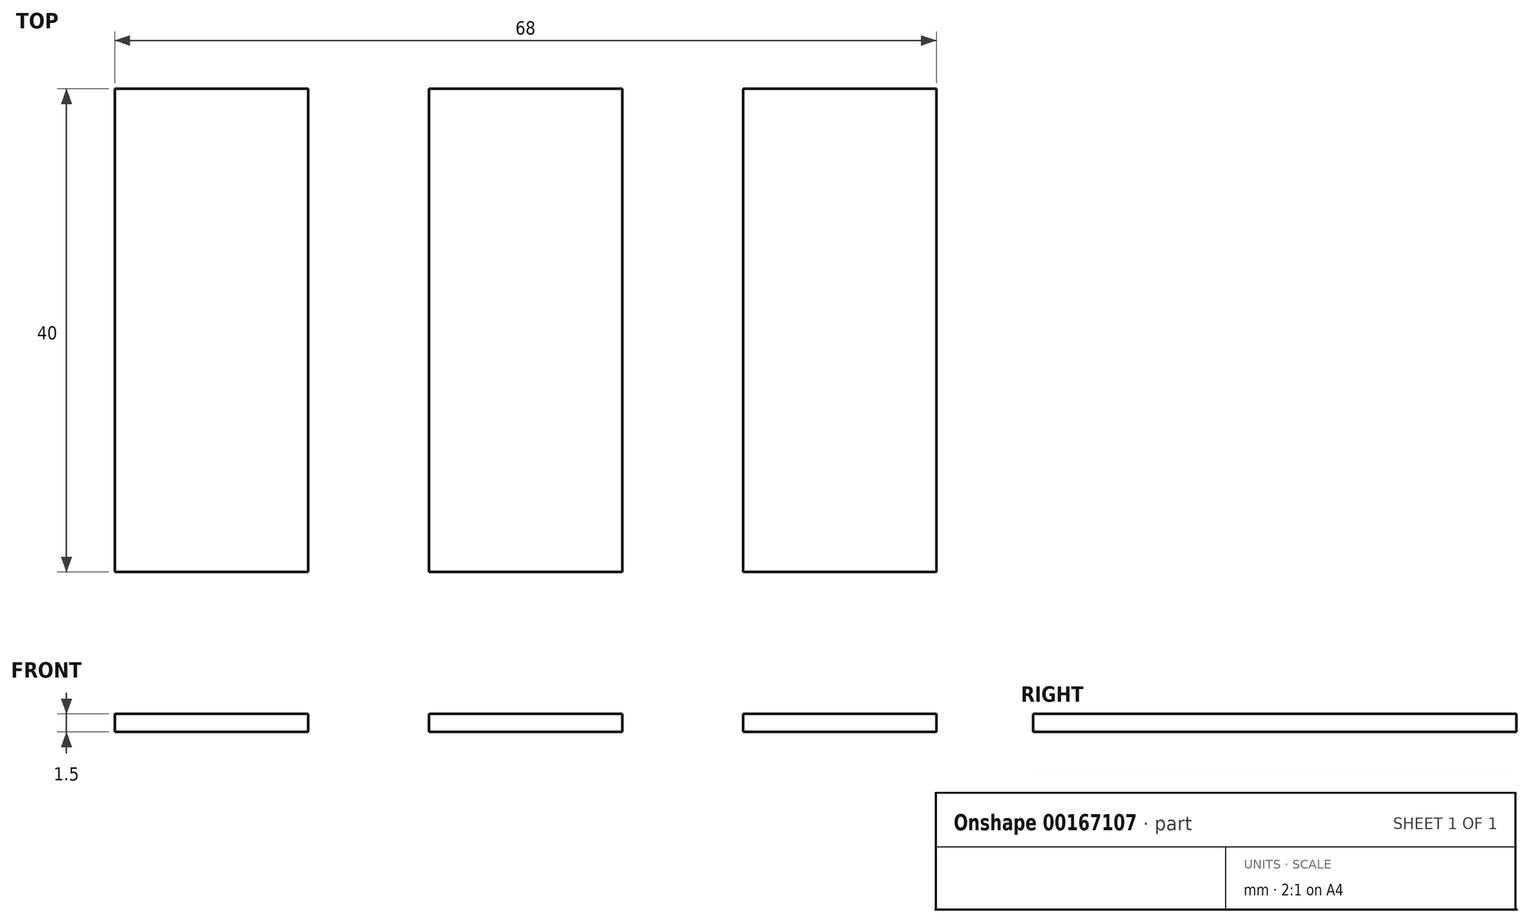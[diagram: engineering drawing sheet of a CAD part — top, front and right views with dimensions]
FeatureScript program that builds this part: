
annotation { "Feature Type Name" : "Feature", "Feature Type Description" : "" }
export const myFeature = defineFeature(function(context is Context, id is Id, definition is map)
    precondition{}
    {
        {
            var Q0;
            Q0=qCreatedBy(makeId("Top.planeOp"),FACE);
            var sketch = newSketch(context, id + "F0", { "sketchPlane" : qUnion([Q0])});
            skLineSegment(sketch, "E0.bottom", {"start": v(-8, 20) * mm, "end": v(8, 20) * mm});
            skLineSegment(sketch, "E0.top", {"start": v(-8, -20) * mm, "end": v(8, -20) * mm});
            skLineSegment(sketch, "E0.left", {"start": v(-8, 20) * mm, "end": v(-8, -20) * mm});
            skLineSegment(sketch, "E0.right", {"start": v(8, 20) * mm, "end": v(8, -20) * mm});
            skLineSegment(sketch, "E1.bottom", {"start": v(-18, 20) * mm, "end": v(-34, 20) * mm});
            skLineSegment(sketch, "E1.top", {"start": v(-18, -20) * mm, "end": v(-34, -20) * mm});
            skLineSegment(sketch, "E1.left", {"start": v(-18, 20) * mm, "end": v(-18, -20) * mm});
            skLineSegment(sketch, "E1.right", {"start": v(-34, 20) * mm, "end": v(-34, -20) * mm});
            skLineSegment(sketch, "E2.bottom", {"start": v(18, 20) * mm, "end": v(34, 20) * mm});
            skLineSegment(sketch, "E2.top", {"start": v(18, -20) * mm, "end": v(34, -20) * mm});
            skLineSegment(sketch, "E2.left", {"start": v(18, 20) * mm, "end": v(18, -20) * mm});
            skLineSegment(sketch, "E2.right", {"start": v(34, 20) * mm, "end": v(34, -20) * mm});
            skSolve(sketch);
        }
        {
            var Q0;
            Q0=makeQuery(id+"F0.imprint","IMPRINT",FACE,{"disambiguationData":[TD([[makeQuery(id+"F0.imprint","IMPRINT",EDGE,{"derivedFrom":sQuery(id+"F0.wireOp",EDGE,"E1.bottom")}),1.0]])]});
            extrude(context, id + "F1", {"entities" : qUnion([Q0]), "depth" : 1.5 * mm});
        }
        {
            var Q0;
            Q0=makeQuery(id+"F0.imprint","IMPRINT",FACE,{"disambiguationData":[TD([[makeQuery(id+"F0.imprint","IMPRINT",EDGE,{"derivedFrom":sQuery(id+"F0.wireOp",EDGE,"E0.bottom")}),-1.0]])]});
            extrude(context, id + "F2", {"entities" : qUnion([Q0]), "depth" : 1.5 * mm});
        }
        {
            var Q0;
            Q0=makeQuery(id+"F0.imprint","IMPRINT",FACE,{"disambiguationData":[TD([[makeQuery(id+"F0.imprint","IMPRINT",EDGE,{"derivedFrom":sQuery(id+"F0.wireOp",EDGE,"E2.bottom")}),-1.0]])]});
            extrude(context, id + "F3", {"entities" : qUnion([Q0]), "depth" : 1.5 * mm});
        }
    });
